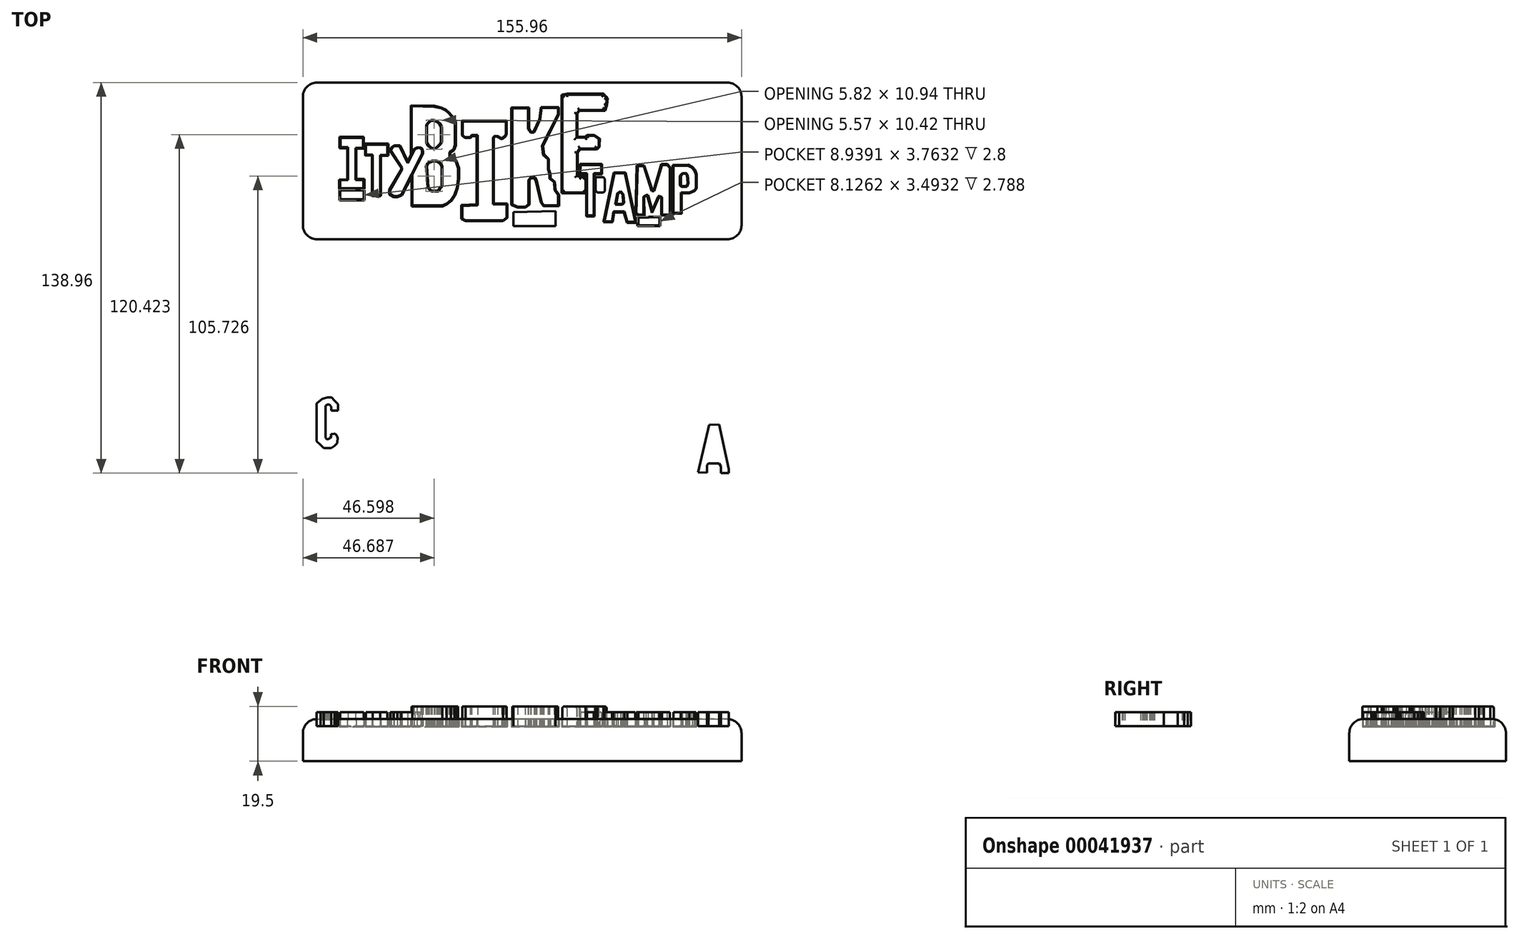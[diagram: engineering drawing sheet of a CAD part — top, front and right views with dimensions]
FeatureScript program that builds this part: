
annotation { "Feature Type Name" : "Feature", "Feature Type Description" : "" }
export const myFeature = defineFeature(function(context is Context, id is Id, definition is map)
    precondition{}
    {
        {
            var Q0;
            Q0=qCreatedBy(makeId("Top.planeOp"),FACE);
            var sketch = newSketch(context, id + "F0", { "sketchPlane" : qUnion([Q0])});
            skLineSegment(sketch, "E0", {"start": v(7.3, -128.71) * mm, "end": v(7.3, -128.71) * mm});
            skLineSegment(sketch, "E1", {"start": v(7.3, -128.71) * mm, "end": v(6.42, -129.66) * mm});
            skLineSegment(sketch, "E2", {"start": v(6.42, -129.66) * mm, "end": v(5.21, -130.33) * mm});
            skLineSegment(sketch, "E3", {"start": v(5.21, -130.33) * mm, "end": v(2.52, -130.33) * mm});
            skLineSegment(sketch, "E4", {"start": v(2.52, -130.33) * mm, "end": v(1.45, -129.25) * mm});
            skLineSegment(sketch, "E5", {"start": v(1.45, -129.25) * mm, "end": v(0, -127.97) * mm});
            skLineSegment(sketch, "E6", {"start": v(0, -127.97) * mm, "end": v(0, -127.17) * mm});
            skLineSegment(sketch, "E7", {"start": v(0, -127.17) * mm, "end": v(0, -114.52) * mm});
            skLineSegment(sketch, "E8", {"start": v(0, -114.52) * mm, "end": v(2.03, -112.78) * mm});
            skLineSegment(sketch, "E9", {"start": v(2.03, -112.78) * mm, "end": v(2.07, -112.78) * mm});
            skLineSegment(sketch, "E10", {"start": v(2.07, -112.78) * mm, "end": v(3.94, -112.3) * mm});
            skLineSegment(sketch, "E11", {"start": v(3.94, -112.3) * mm, "end": v(5.35, -112.3) * mm});
            skLineSegment(sketch, "E12", {"start": v(5.35, -112.3) * mm, "end": v(6.42, -113.45) * mm});
            skLineSegment(sketch, "E13", {"start": v(6.42, -113.45) * mm, "end": v(7.7, -114.73) * mm});
            skLineSegment(sketch, "E14", {"start": v(7.7, -114.73) * mm, "end": v(7.7, -116.34) * mm});
            skLineSegment(sketch, "E15", {"start": v(7.7, -116.34) * mm, "end": v(7.7, -117.01) * mm});
            skLineSegment(sketch, "E16", {"start": v(7.7, -117.01) * mm, "end": v(5.28, -117.01) * mm});
            skLineSegment(sketch, "E17", {"start": v(5.28, -117.01) * mm, "end": v(5.28, -115.6) * mm});
            skLineSegment(sketch, "E18", {"start": v(5.28, -115.6) * mm, "end": v(4.54, -114.9) * mm});
            skLineSegment(sketch, "E19", {"start": v(4.54, -114.9) * mm, "end": v(3.94, -114.9) * mm});
            skLineSegment(sketch, "E20", {"start": v(3.94, -114.9) * mm, "end": v(3.26, -115.27) * mm});
            skLineSegment(sketch, "E21", {"start": v(3.26, -115.27) * mm, "end": v(3.26, -115.7) * mm});
            skLineSegment(sketch, "E22", {"start": v(3.26, -115.7) * mm, "end": v(3.26, -126.66) * mm});
            skLineSegment(sketch, "E23", {"start": v(3.26, -126.66) * mm, "end": v(3.58, -127.14) * mm});
            skLineSegment(sketch, "E24", {"start": v(3.58, -127.14) * mm, "end": v(4.1, -127.14) * mm});
            skLineSegment(sketch, "E25", {"start": v(4.1, -127.14) * mm, "end": v(4.9, -126.82) * mm});
            skLineSegment(sketch, "E26", {"start": v(4.9, -126.82) * mm, "end": v(5.18, -126.18) * mm});
            skLineSegment(sketch, "E27", {"start": v(5.18, -126.18) * mm, "end": v(5.14, -125.38) * mm});
            skLineSegment(sketch, "E28", {"start": v(5.14, -125.38) * mm, "end": v(6.06, -125.34) * mm});
            skLineSegment(sketch, "E29", {"start": v(6.06, -125.34) * mm, "end": v(6.58, -125.34) * mm});
            skLineSegment(sketch, "E30", {"start": v(6.58, -125.34) * mm, "end": v(7.14, -125.82) * mm});
            skLineSegment(sketch, "E31", {"start": v(7.14, -125.82) * mm, "end": v(7.54, -126.82) * mm});
            skLineSegment(sketch, "E32", {"start": v(7.54, -126.82) * mm, "end": v(7.45, -128.26) * mm});
            skLineSegment(sketch, "E33", {"start": v(7.45, -128.26) * mm, "end": v(7.3, -128.71) * mm});
            skLineSegment(sketch, "E34", {"start": v(8.43, -38.73) * mm, "end": v(8.43, -41.9) * mm});
            skLineSegment(sketch, "E35", {"start": v(8.43, -41.9) * mm, "end": v(16.77, -41.9) * mm});
            skLineSegment(sketch, "E36", {"start": v(16.77, -41.9) * mm, "end": v(16.77, -38.8) * mm});
            skLineSegment(sketch, "E37", {"start": v(16.77, -38.8) * mm, "end": v(8.43, -38.73) * mm});
            skLineSegment(sketch, "E38", {"start": v(8.4, -35.1) * mm, "end": v(8.4, -37.86) * mm});
            skLineSegment(sketch, "E39", {"start": v(8.4, -37.86) * mm, "end": v(16.72, -37.86) * mm});
            skLineSegment(sketch, "E40", {"start": v(16.72, -37.86) * mm, "end": v(16.72, -34.97) * mm});
            skLineSegment(sketch, "E41", {"start": v(16.72, -34.97) * mm, "end": v(13.88, -34.97) * mm});
            skLineSegment(sketch, "E42", {"start": v(13.88, -34.97) * mm, "end": v(13.88, -23.55) * mm});
            skLineSegment(sketch, "E43", {"start": v(13.88, -23.55) * mm, "end": v(16.48, -23.55) * mm});
            skLineSegment(sketch, "E44", {"start": v(16.48, -23.55) * mm, "end": v(16.48, -19.95) * mm});
            skLineSegment(sketch, "E45", {"start": v(16.48, -19.95) * mm, "end": v(8.48, -19.95) * mm});
            skLineSegment(sketch, "E46", {"start": v(8.48, -19.95) * mm, "end": v(8.48, -23.35) * mm});
            skLineSegment(sketch, "E47", {"start": v(8.48, -23.35) * mm, "end": v(11.24, -23.35) * mm});
            skLineSegment(sketch, "E48", {"start": v(11.24, -23.35) * mm, "end": v(11.24, -34.99) * mm});
            skLineSegment(sketch, "E49", {"start": v(11.24, -34.99) * mm, "end": v(8.4, -35.1) * mm});
            skLineSegment(sketch, "E50", {"start": v(19.96, -25.92) * mm, "end": v(19.96, -40.42) * mm});
            skLineSegment(sketch, "E51", {"start": v(19.96, -40.42) * mm, "end": v(22.65, -40.42) * mm});
            skLineSegment(sketch, "E52", {"start": v(22.65, -40.42) * mm, "end": v(22.65, -26.04) * mm});
            skLineSegment(sketch, "E53", {"start": v(22.65, -26.04) * mm, "end": v(25.23, -26.04) * mm});
            skLineSegment(sketch, "E54", {"start": v(25.23, -26.04) * mm, "end": v(25.23, -22.39) * mm});
            skLineSegment(sketch, "E55", {"start": v(25.23, -22.39) * mm, "end": v(17.56, -22.39) * mm});
            skLineSegment(sketch, "E56", {"start": v(17.56, -22.39) * mm, "end": v(17.56, -25.98) * mm});
            skLineSegment(sketch, "E57", {"start": v(17.56, -25.98) * mm, "end": v(19.96, -25.92) * mm});
            skLineSegment(sketch, "E58", {"start": v(26.38, -24.56) * mm, "end": v(30.4, -30.61) * mm});
            skLineSegment(sketch, "E59", {"start": v(30.4, -30.61) * mm, "end": v(30.4, -31.35) * mm});
            skLineSegment(sketch, "E60", {"start": v(30.4, -31.35) * mm, "end": v(26.16, -38.64) * mm});
            skLineSegment(sketch, "E61", {"start": v(26.16, -38.64) * mm, "end": v(26.16, -39.89) * mm});
            skLineSegment(sketch, "E62", {"start": v(26.16, -39.89) * mm, "end": v(27.52, -40.73) * mm});
            skLineSegment(sketch, "E63", {"start": v(27.52, -40.73) * mm, "end": v(28.7, -40.73) * mm});
            skLineSegment(sketch, "E64", {"start": v(28.7, -40.73) * mm, "end": v(30.14, -40.16) * mm});
            skLineSegment(sketch, "E65", {"start": v(30.14, -40.16) * mm, "end": v(37.54, -25.76) * mm});
            skLineSegment(sketch, "E66", {"start": v(37.54, -25.76) * mm, "end": v(37.54, -24.3) * mm});
            skLineSegment(sketch, "E67", {"start": v(37.54, -24.3) * mm, "end": v(36.73, -23.6) * mm});
            skLineSegment(sketch, "E68", {"start": v(36.73, -23.6) * mm, "end": v(36.05, -23.6) * mm});
            skLineSegment(sketch, "E69", {"start": v(36.05, -23.6) * mm, "end": v(34.98, -24.05) * mm});
            skLineSegment(sketch, "E70", {"start": v(34.98, -24.05) * mm, "end": v(32.38, -28.97) * mm});
            skLineSegment(sketch, "E71", {"start": v(32.38, -28.97) * mm, "end": v(29.5, -22.92) * mm});
            skLineSegment(sketch, "E72", {"start": v(29.5, -22.92) * mm, "end": v(28.5, -22.92) * mm});
            skLineSegment(sketch, "E73", {"start": v(28.5, -22.92) * mm, "end": v(27.65, -22.92) * mm});
            skLineSegment(sketch, "E74", {"start": v(27.65, -22.92) * mm, "end": v(26.84, -23.64) * mm});
            skLineSegment(sketch, "E75", {"start": v(26.84, -23.64) * mm, "end": v(26.38, -24.56) * mm});
            skLineSegment(sketch, "E76", {"start": v(33.84, -8.7) * mm, "end": v(33.84, -25.36) * mm});
            skPoint(sketch, "E76.startSnap0", {"position": v(33.84, -32.96) * mm});
            skLineSegment(sketch, "E77", {"start": v(33.84, -25.36) * mm, "end": v(34.75, -23.9) * mm});
            skLineSegment(sketch, "E78", {"start": v(34.75, -23.9) * mm, "end": v(35.76, -23.4) * mm});
            skLineSegment(sketch, "E79", {"start": v(35.76, -23.4) * mm, "end": v(37.08, -23.4) * mm});
            skLineSegment(sketch, "E80", {"start": v(37.08, -23.4) * mm, "end": v(37.54, -23.71) * mm});
            skLineSegment(sketch, "E81", {"start": v(37.54, -23.71) * mm, "end": v(37.88, -24.87) * mm});
            skLineSegment(sketch, "E82", {"start": v(37.88, -24.87) * mm, "end": v(37.88, -25.61) * mm});
            skLineSegment(sketch, "E83", {"start": v(37.88, -25.61) * mm, "end": v(34.05, -32.96) * mm});
            skLineSegment(sketch, "E84", {"start": v(34.05, -32.96) * mm, "end": v(34.05, -44.03) * mm});
            skLineSegment(sketch, "E85", {"start": v(34.05, -44.03) * mm, "end": v(44.78, -44.03) * mm});
            skLineSegment(sketch, "E86", {"start": v(44.78, -44.03) * mm, "end": v(46.22, -43.31) * mm});
            skLineSegment(sketch, "E87", {"start": v(46.22, -43.31) * mm, "end": v(47.78, -42.11) * mm});
            skLineSegment(sketch, "E88", {"start": v(47.78, -42.11) * mm, "end": v(49.04, -40.26) * mm});
            skLineSegment(sketch, "E89", {"start": v(49.04, -40.26) * mm, "end": v(49.88, -37.68) * mm});
            skLineSegment(sketch, "E90", {"start": v(49.88, -37.68) * mm, "end": v(50.36, -34.5) * mm});
            skLineSegment(sketch, "E91", {"start": v(50.36, -34.5) * mm, "end": v(50.36, -30.8) * mm});
            skLineSegment(sketch, "E92", {"start": v(50.36, -30.8) * mm, "end": v(49.4, -28.15) * mm});
            skLineSegment(sketch, "E93", {"start": v(49.4, -28.15) * mm, "end": v(48.02, -26.78) * mm});
            skLineSegment(sketch, "E94", {"start": v(48.02, -26.78) * mm, "end": v(47.24, -26.78) * mm});
            skLineSegment(sketch, "E95", {"start": v(47.24, -26.78) * mm, "end": v(47.24, -25.04) * mm});
            skLineSegment(sketch, "E96", {"start": v(47.24, -25.04) * mm, "end": v(48.62, -24.14) * mm});
            skLineSegment(sketch, "E97", {"start": v(48.62, -24.14) * mm, "end": v(49.22, -22.58) * mm});
            skLineSegment(sketch, "E98", {"start": v(49.22, -22.58) * mm, "end": v(49.22, -14.31) * mm});
            skLineSegment(sketch, "E99", {"start": v(49.22, -14.31) * mm, "end": v(48.44, -12.88) * mm});
            skLineSegment(sketch, "E100", {"start": v(48.44, -12.88) * mm, "end": v(47, -11.2) * mm});
            skLineSegment(sketch, "E101", {"start": v(47, -11.2) * mm, "end": v(45.86, -10.24) * mm});
            skLineSegment(sketch, "E102", {"start": v(45.86, -10.24) * mm, "end": v(44.3, -9.46) * mm});
            skLineSegment(sketch, "E103", {"start": v(44.3, -9.46) * mm, "end": v(41.85, -8.92) * mm});
            skLineSegment(sketch, "E104", {"start": v(41.85, -8.92) * mm, "end": v(33.84, -8.7) * mm});
            skLineSegment(sketch, "E105", {"start": v(38.97, -15.33) * mm, "end": v(38.97, -21.8) * mm});
            skLineSegment(sketch, "E106", {"start": v(38.97, -21.8) * mm, "end": v(39.7, -22.88) * mm});
            skLineSegment(sketch, "E107", {"start": v(39.7, -22.88) * mm, "end": v(40.89, -23.78) * mm});
            skLineSegment(sketch, "E108", {"start": v(40.89, -23.78) * mm, "end": v(42.09, -24.08) * mm});
            skLineSegment(sketch, "E109", {"start": v(42.09, -24.08) * mm, "end": v(43.23, -23.18) * mm});
            skLineSegment(sketch, "E110", {"start": v(43.23, -23.18) * mm, "end": v(44.13, -22.28) * mm});
            skLineSegment(sketch, "E111", {"start": v(44.13, -22.28) * mm, "end": v(44.54, -21.44) * mm});
            skLineSegment(sketch, "E112", {"start": v(44.54, -21.44) * mm, "end": v(44.54, -16.11) * mm});
            skLineSegment(sketch, "E113", {"start": v(44.54, -16.11) * mm, "end": v(43.83, -14.8) * mm});
            skLineSegment(sketch, "E114", {"start": v(43.83, -14.8) * mm, "end": v(43.05, -14.2) * mm});
            skLineSegment(sketch, "E115", {"start": v(43.05, -14.2) * mm, "end": v(41.79, -13.65) * mm});
            skLineSegment(sketch, "E116", {"start": v(41.79, -13.65) * mm, "end": v(40.65, -13.65) * mm});
            skLineSegment(sketch, "E117", {"start": v(40.65, -13.65) * mm, "end": v(39.7, -14.5) * mm});
            skLineSegment(sketch, "E118", {"start": v(39.7, -14.5) * mm, "end": v(38.97, -15.33) * mm});
            skLineSegment(sketch, "E119", {"start": v(39.47, -37.6) * mm, "end": v(38.94, -30.01) * mm});
            skLineSegment(sketch, "E120", {"start": v(38.94, -30.01) * mm, "end": v(39.58, -28.84) * mm});
            skLineSegment(sketch, "E121", {"start": v(39.58, -28.84) * mm, "end": v(41.07, -28.1) * mm});
            skLineSegment(sketch, "E122", {"start": v(41.07, -28.1) * mm, "end": v(42.73, -28.1) * mm});
            skLineSegment(sketch, "E123", {"start": v(42.73, -28.1) * mm, "end": v(44.33, -29.16) * mm});
            skLineSegment(sketch, "E124", {"start": v(44.33, -29.16) * mm, "end": v(44.76, -30.17) * mm});
            skLineSegment(sketch, "E125", {"start": v(44.76, -30.17) * mm, "end": v(44.76, -37.33) * mm});
            skLineSegment(sketch, "E126", {"start": v(44.76, -37.33) * mm, "end": v(44.06, -37.91) * mm});
            skLineSegment(sketch, "E127", {"start": v(44.06, -37.91) * mm, "end": v(43.42, -39.04) * mm});
            skLineSegment(sketch, "E128", {"start": v(43.42, -39.04) * mm, "end": v(40.75, -39.04) * mm});
            skLineSegment(sketch, "E129", {"start": v(40.75, -39.04) * mm, "end": v(40.06, -38.34) * mm});
            skLineSegment(sketch, "E130", {"start": v(40.06, -38.34) * mm, "end": v(39.47, -37.6) * mm});
            skLineSegment(sketch, "E131", {"start": v(51.83, -44.2) * mm, "end": v(51.83, -48.63) * mm});
            skLineSegment(sketch, "E132", {"start": v(51.83, -48.63) * mm, "end": v(53.03, -49.35) * mm});
            skLineSegment(sketch, "E133", {"start": v(53.03, -49.35) * mm, "end": v(66.27, -49.35) * mm});
            skLineSegment(sketch, "E134", {"start": v(66.27, -49.35) * mm, "end": v(67.59, -48.33) * mm});
            skLineSegment(sketch, "E135", {"start": v(67.59, -48.33) * mm, "end": v(67.59, -43.66) * mm});
            skLineSegment(sketch, "E136", {"start": v(67.59, -43.66) * mm, "end": v(62.74, -43.66) * mm});
            skLineSegment(sketch, "E137", {"start": v(62.74, -43.66) * mm, "end": v(62.74, -19.81) * mm});
            skLineSegment(sketch, "E138", {"start": v(62.74, -19.81) * mm, "end": v(63.4, -19.21) * mm});
            skLineSegment(sketch, "E139", {"start": v(63.4, -19.21) * mm, "end": v(64.35, -19.33) * mm});
            skLineSegment(sketch, "E140", {"start": v(64.35, -19.33) * mm, "end": v(65.85, -20.17) * mm});
            skLineSegment(sketch, "E141", {"start": v(65.85, -20.17) * mm, "end": v(66.87, -19.4) * mm});
            skLineSegment(sketch, "E142", {"start": v(66.87, -19.4) * mm, "end": v(67.3, -18.73) * mm});
            skLineSegment(sketch, "E143", {"start": v(67.3, -18.73) * mm, "end": v(67.3, -14.18) * mm});
            skLineSegment(sketch, "E144", {"start": v(67.3, -14.18) * mm, "end": v(52.01, -14.18) * mm});
            skLineSegment(sketch, "E145", {"start": v(52.01, -14.18) * mm, "end": v(52.01, -19.03) * mm});
            skLineSegment(sketch, "E146", {"start": v(52.01, -19.03) * mm, "end": v(52.8, -19.7) * mm});
            skLineSegment(sketch, "E147", {"start": v(52.8, -19.7) * mm, "end": v(54.59, -19.7) * mm});
            skLineSegment(sketch, "E148", {"start": v(54.59, -19.7) * mm, "end": v(55.13, -19.03) * mm});
            skLineSegment(sketch, "E149", {"start": v(55.13, -19.03) * mm, "end": v(57.28, -19.03) * mm});
            skLineSegment(sketch, "E150", {"start": v(57.28, -19.03) * mm, "end": v(57.28, -43.24) * mm});
            skLineSegment(sketch, "E151", {"start": v(57.28, -43.24) * mm, "end": v(57.28, -43.96) * mm});
            skLineSegment(sketch, "E152", {"start": v(57.28, -43.96) * mm, "end": v(51.83, -44.2) * mm});
            skLineSegment(sketch, "E153", {"start": v(70, -46.39) * mm, "end": v(70, -51.38) * mm});
            skLineSegment(sketch, "E154", {"start": v(70, -51.38) * mm, "end": v(84.93, -51.38) * mm});
            skLineSegment(sketch, "E155", {"start": v(84.93, -51.38) * mm, "end": v(84.93, -46.06) * mm});
            skLineSegment(sketch, "E156", {"start": v(84.93, -46.06) * mm, "end": v(70, -46.39) * mm});
            skLineSegment(sketch, "E157", {"start": v(69.57, -43.68) * mm, "end": v(69.57, -9.49) * mm});
            skLineSegment(sketch, "E158", {"start": v(69.57, -9.49) * mm, "end": v(75.23, -9.49) * mm});
            skLineSegment(sketch, "E159", {"start": v(75.23, -9.49) * mm, "end": v(75.23, -15.86) * mm});
            skLineSegment(sketch, "E160", {"start": v(75.23, -15.86) * mm, "end": v(75.23, -16.76) * mm});
            skLineSegment(sketch, "E161", {"start": v(75.23, -16.76) * mm, "end": v(76.09, -18.1) * mm});
            skLineSegment(sketch, "E162", {"start": v(76.09, -18.1) * mm, "end": v(77.32, -18.1) * mm});
            skLineSegment(sketch, "E163", {"start": v(77.32, -18.1) * mm, "end": v(79.51, -13.34) * mm});
            skLineSegment(sketch, "E164", {"start": v(79.51, -13.34) * mm, "end": v(80.08, -9.4) * mm});
            skLineSegment(sketch, "E165", {"start": v(80.08, -9.4) * mm, "end": v(85.88, -9.4) * mm});
            skLineSegment(sketch, "E166", {"start": v(85.88, -9.4) * mm, "end": v(85.88, -11.63) * mm});
            skLineSegment(sketch, "E167", {"start": v(85.88, -11.63) * mm, "end": v(80.22, -22.76) * mm});
            skLineSegment(sketch, "E168", {"start": v(80.22, -22.76) * mm, "end": v(80.6, -26.04) * mm});
            skLineSegment(sketch, "E169", {"start": v(80.6, -26.04) * mm, "end": v(82.32, -27.6) * mm});
            skLineSegment(sketch, "E170", {"start": v(82.32, -27.6) * mm, "end": v(82.32, -31.22) * mm});
            skLineSegment(sketch, "E171", {"start": v(82.32, -31.22) * mm, "end": v(82.89, -32.84) * mm});
            skLineSegment(sketch, "E172", {"start": v(82.89, -32.84) * mm, "end": v(82.89, -34.45) * mm});
            skLineSegment(sketch, "E173", {"start": v(82.89, -34.45) * mm, "end": v(84.46, -35.74) * mm});
            skLineSegment(sketch, "E174", {"start": v(84.46, -35.74) * mm, "end": v(84.65, -38.6) * mm});
            skLineSegment(sketch, "E175", {"start": v(84.65, -38.6) * mm, "end": v(85.93, -40.3) * mm});
            skLineSegment(sketch, "E176", {"start": v(85.93, -40.3) * mm, "end": v(85.93, -43.96) * mm});
            skLineSegment(sketch, "E177", {"start": v(85.93, -43.96) * mm, "end": v(80.84, -43.96) * mm});
            skLineSegment(sketch, "E178", {"start": v(80.84, -43.96) * mm, "end": v(80.08, -42.87) * mm});
            skLineSegment(sketch, "E179", {"start": v(80.08, -42.87) * mm, "end": v(78.23, -34.93) * mm});
            skLineSegment(sketch, "E180", {"start": v(78.23, -34.93) * mm, "end": v(77.7, -34.03) * mm});
            skLineSegment(sketch, "E181", {"start": v(77.7, -34.03) * mm, "end": v(76.75, -34.03) * mm});
            skLineSegment(sketch, "E182", {"start": v(76.75, -34.03) * mm, "end": v(76.18, -34.03) * mm});
            skLineSegment(sketch, "E183", {"start": v(76.18, -34.03) * mm, "end": v(75.37, -34.93) * mm});
            skLineSegment(sketch, "E184", {"start": v(75.37, -34.93) * mm, "end": v(75.37, -43.63) * mm});
            skLineSegment(sketch, "E185", {"start": v(75.37, -43.63) * mm, "end": v(74.23, -44.49) * mm});
            skLineSegment(sketch, "E186", {"start": v(74.23, -44.49) * mm, "end": v(71.57, -44.49) * mm});
            skLineSegment(sketch, "E187", {"start": v(71.57, -44.49) * mm, "end": v(69.57, -43.68) * mm});
            skLineSegment(sketch, "E188", {"start": v(87.4, -4.91) * mm, "end": v(87.4, -39.4) * mm});
            skLineSegment(sketch, "E189", {"start": v(87.4, -39.4) * mm, "end": v(95.63, -39.4) * mm});
            skLineSegment(sketch, "E190", {"start": v(95.63, -39.4) * mm, "end": v(95.63, -33.97) * mm});
            skLineSegment(sketch, "E191", {"start": v(95.63, -33.97) * mm, "end": v(93.82, -33.97) * mm});
            skLineSegment(sketch, "E192", {"start": v(93.82, -33.97) * mm, "end": v(92.61, -33.52) * mm});
            skLineSegment(sketch, "E193", {"start": v(92.61, -33.52) * mm, "end": v(92.61, -25.3) * mm});
            skLineSegment(sketch, "E194", {"start": v(92.61, -25.3) * mm, "end": v(93.6, -23.7) * mm});
            skLineSegment(sketch, "E195", {"start": v(93.6, -23.7) * mm, "end": v(99.33, -23.78) * mm});
            skLineSegment(sketch, "E196", {"start": v(99.33, -23.78) * mm, "end": v(100.31, -23.25) * mm});
            skLineSegment(sketch, "E197", {"start": v(100.31, -23.25) * mm, "end": v(100.39, -20.39) * mm});
            skLineSegment(sketch, "E198", {"start": v(100.39, -20.39) * mm, "end": v(98.73, -19.25) * mm});
            skLineSegment(sketch, "E199", {"start": v(98.73, -19.25) * mm, "end": v(96.24, -19.25) * mm});
            skLineSegment(sketch, "E200", {"start": v(96.24, -19.25) * mm, "end": v(95.63, -19.86) * mm});
            skLineSegment(sketch, "E201", {"start": v(95.63, -19.86) * mm, "end": v(92.46, -19.86) * mm});
            skLineSegment(sketch, "E202", {"start": v(92.46, -19.86) * mm, "end": v(92.46, -11.33) * mm});
            skLineSegment(sketch, "E203", {"start": v(92.46, -11.33) * mm, "end": v(93.37, -10.04) * mm});
            skLineSegment(sketch, "E204", {"start": v(93.37, -10.04) * mm, "end": v(102.43, -10.04) * mm});
            skLineSegment(sketch, "E205", {"start": v(102.43, -10.04) * mm, "end": v(103.03, -8.23) * mm});
            skLineSegment(sketch, "E206", {"start": v(103.03, -8.23) * mm, "end": v(103.18, -5.97) * mm});
            skLineSegment(sketch, "E207", {"start": v(103.18, -5.97) * mm, "end": v(101.97, -4.6) * mm});
            skLineSegment(sketch, "E208", {"start": v(101.97, -4.6) * mm, "end": v(89.07, -4.6) * mm});
            skLineSegment(sketch, "E209", {"start": v(89.07, -4.6) * mm, "end": v(87.4, -4.91) * mm});
            skLineSegment(sketch, "E210", {"start": v(99.86, -39.47) * mm, "end": v(99.18, -38.64) * mm});
            skLineSegment(sketch, "E211", {"start": v(99.18, -38.64) * mm, "end": v(99.18, -34.03) * mm});
            skLineSegment(sketch, "E212", {"start": v(99.18, -34.03) * mm, "end": v(101.98, -34.03) * mm});
            skLineSegment(sketch, "E213", {"start": v(101.98, -34.03) * mm, "end": v(102.58, -34.6) * mm});
            skLineSegment(sketch, "E214", {"start": v(102.58, -34.6) * mm, "end": v(102.58, -38.94) * mm});
            skLineSegment(sketch, "E215", {"start": v(102.58, -38.94) * mm, "end": v(102.01, -39.43) * mm});
            skLineSegment(sketch, "E216", {"start": v(102.01, -39.43) * mm, "end": v(99.86, -39.47) * mm});
            skLineSegment(sketch, "E217", {"start": v(93.75, -32.52) * mm, "end": v(96.16, -32.52) * mm});
            skLineSegment(sketch, "E218", {"start": v(96.16, -32.52) * mm, "end": v(96.16, -47.58) * mm});
            skLineSegment(sketch, "E219", {"start": v(96.16, -47.58) * mm, "end": v(98.54, -47.58) * mm});
            skLineSegment(sketch, "E220", {"start": v(98.54, -47.58) * mm, "end": v(98.54, -32.63) * mm});
            skLineSegment(sketch, "E221", {"start": v(98.54, -32.63) * mm, "end": v(101.26, -32.63) * mm});
            skLineSegment(sketch, "E222", {"start": v(101.26, -32.63) * mm, "end": v(101.26, -29.61) * mm});
            skLineSegment(sketch, "E223", {"start": v(101.26, -29.61) * mm, "end": v(93.86, -29.61) * mm});
            skLineSegment(sketch, "E224", {"start": v(93.86, -29.61) * mm, "end": v(93.75, -32.52) * mm});
            skLineSegment(sketch, "E225", {"start": v(102.34, -49.66) * mm, "end": v(105.11, -49.66) * mm});
            skLineSegment(sketch, "E226", {"start": v(105.11, -49.66) * mm, "end": v(105.6, -46.2) * mm});
            skLineSegment(sketch, "E227", {"start": v(105.6, -46.2) * mm, "end": v(109.49, -46.2) * mm});
            skLineSegment(sketch, "E228", {"start": v(109.49, -46.2) * mm, "end": v(110.56, -49.88) * mm});
            skLineSegment(sketch, "E229", {"start": v(110.56, -49.88) * mm, "end": v(113.28, -49.88) * mm});
            skLineSegment(sketch, "E230", {"start": v(113.28, -49.88) * mm, "end": v(109.6, -32.58) * mm});
            skLineSegment(sketch, "E231", {"start": v(109.6, -32.58) * mm, "end": v(105.96, -32.58) * mm});
            skLineSegment(sketch, "E232", {"start": v(105.96, -32.58) * mm, "end": v(102.34, -49.66) * mm});
            skLineSegment(sketch, "E233", {"start": v(106.18, -43.74) * mm, "end": v(108.8, -43.74) * mm});
            skLineSegment(sketch, "E234", {"start": v(108.8, -43.74) * mm, "end": v(109.33, -43.15) * mm});
            skLineSegment(sketch, "E235", {"start": v(109.33, -43.15) * mm, "end": v(109.17, -40.05) * mm});
            skLineSegment(sketch, "E236", {"start": v(109.17, -40.05) * mm, "end": v(108.1, -38.88) * mm});
            skLineSegment(sketch, "E237", {"start": v(108.1, -38.88) * mm, "end": v(106.93, -39.68) * mm});
            skLineSegment(sketch, "E238", {"start": v(106.93, -39.68) * mm, "end": v(106.18, -43.74) * mm});
            skLineSegment(sketch, "E239", {"start": v(114.4, -48.49) * mm, "end": v(114.4, -51.1) * mm});
            skLineSegment(sketch, "E240", {"start": v(114.4, -51.1) * mm, "end": v(121.92, -51.1) * mm});
            skLineSegment(sketch, "E241", {"start": v(121.92, -51.1) * mm, "end": v(121.92, -48.22) * mm});
            skLineSegment(sketch, "E242", {"start": v(121.92, -48.22) * mm, "end": v(114.4, -48.49) * mm});
            skLineSegment(sketch, "E243", {"start": v(113.7, -46.67) * mm, "end": v(114.4, -47.37) * mm});
            skLineSegment(sketch, "E244", {"start": v(114.4, -47.37) * mm, "end": v(116.27, -47.37) * mm});
            skLineSegment(sketch, "E245", {"start": v(116.27, -47.37) * mm, "end": v(116.21, -41.02) * mm});
            skLineSegment(sketch, "E246", {"start": v(116.21, -41.02) * mm, "end": v(117.07, -40.37) * mm});
            skLineSegment(sketch, "E247", {"start": v(117.07, -40.37) * mm, "end": v(117.87, -40.37) * mm});
            skLineSegment(sketch, "E248", {"start": v(117.87, -40.37) * mm, "end": v(119.36, -45.77) * mm});
            skLineSegment(sketch, "E249", {"start": v(119.36, -45.77) * mm, "end": v(121.44, -41.02) * mm});
            skLineSegment(sketch, "E250", {"start": v(121.44, -41.02) * mm, "end": v(122.14, -40.54) * mm});
            skLineSegment(sketch, "E251", {"start": v(122.14, -40.54) * mm, "end": v(122.83, -41.12) * mm});
            skLineSegment(sketch, "E252", {"start": v(122.83, -41.12) * mm, "end": v(122.83, -47.31) * mm});
            skLineSegment(sketch, "E253", {"start": v(122.83, -47.31) * mm, "end": v(125.6, -47.31) * mm});
            skLineSegment(sketch, "E254", {"start": v(125.6, -47.31) * mm, "end": v(125.6, -30.66) * mm});
            skLineSegment(sketch, "E255", {"start": v(125.6, -30.66) * mm, "end": v(124.6, -29.6) * mm});
            skLineSegment(sketch, "E256", {"start": v(124.6, -29.6) * mm, "end": v(122.78, -29.6) * mm});
            skLineSegment(sketch, "E257", {"start": v(122.78, -29.6) * mm, "end": v(120.1, -38.88) * mm});
            skLineSegment(sketch, "E258", {"start": v(120.1, -38.88) * mm, "end": v(119.16, -38.88) * mm});
            skLineSegment(sketch, "E259", {"start": v(119.16, -38.88) * mm, "end": v(116.32, -30.08) * mm});
            skLineSegment(sketch, "E260", {"start": v(116.32, -30.08) * mm, "end": v(114.16, -30.08) * mm});
            skLineSegment(sketch, "E261", {"start": v(114.16, -30.08) * mm, "end": v(113.7, -46.67) * mm});
            skLineSegment(sketch, "E262", {"start": v(126.94, -46.62) * mm, "end": v(126.94, -29.9) * mm});
            skLineSegment(sketch, "E263", {"start": v(126.94, -29.9) * mm, "end": v(132.15, -29.85) * mm});
            skLineSegment(sketch, "E264", {"start": v(132.15, -29.85) * mm, "end": v(133.4, -30.57) * mm});
            skLineSegment(sketch, "E265", {"start": v(133.4, -30.57) * mm, "end": v(134.43, -31.65) * mm});
            skLineSegment(sketch, "E266", {"start": v(134.43, -31.65) * mm, "end": v(134.9, -33.02) * mm});
            skLineSegment(sketch, "E267", {"start": v(134.9, -33.02) * mm, "end": v(134.9, -37.88) * mm});
            skLineSegment(sketch, "E268", {"start": v(134.9, -37.88) * mm, "end": v(134.25, -38.72) * mm});
            skLineSegment(sketch, "E269", {"start": v(134.25, -38.72) * mm, "end": v(132.57, -39.38) * mm});
            skLineSegment(sketch, "E270", {"start": v(132.57, -39.38) * mm, "end": v(129.51, -39.38) * mm});
            skLineSegment(sketch, "E271", {"start": v(129.51, -39.38) * mm, "end": v(129.51, -46.68) * mm});
            skLineSegment(sketch, "E272", {"start": v(129.51, -46.68) * mm, "end": v(126.94, -46.62) * mm});
            skLineSegment(sketch, "E273", {"start": v(135.68, -139) * mm, "end": v(139.58, -122.16) * mm});
            skLineSegment(sketch, "E274", {"start": v(139.58, -122.16) * mm, "end": v(143.11, -122.04) * mm});
            skLineSegment(sketch, "E275", {"start": v(143.11, -122.04) * mm, "end": v(146.6, -137.86) * mm});
            skLineSegment(sketch, "E276", {"start": v(146.6, -137.86) * mm, "end": v(146.59, -139.3) * mm});
            skLineSegment(sketch, "E277", {"start": v(146.59, -139.3) * mm, "end": v(143.77, -139.26) * mm});
            skLineSegment(sketch, "E278", {"start": v(143.77, -139.26) * mm, "end": v(143.77, -136.9) * mm});
            skLineSegment(sketch, "E279", {"start": v(143.77, -136.9) * mm, "end": v(143.17, -135.88) * mm});
            skLineSegment(sketch, "E280", {"start": v(143.17, -135.88) * mm, "end": v(139.34, -135.88) * mm});
            skLineSegment(sketch, "E281", {"start": v(139.34, -135.88) * mm, "end": v(138.8, -136.48) * mm});
            skLineSegment(sketch, "E282", {"start": v(138.8, -136.48) * mm, "end": v(138.8, -139.11) * mm});
            skLineSegment(sketch, "E283", {"start": v(138.8, -139.11) * mm, "end": v(135.68, -139) * mm});
            skLineSegment(sketch, "E284", {"start": v(139.88, -43.57) * mm, "end": v(139.88, -40.57) * mm});
            skLineSegment(sketch, "E285", {"start": v(139.88, -40.57) * mm, "end": v(140.84, -39.2) * mm});
            skLineSegment(sketch, "E286", {"start": v(140.84, -39.2) * mm, "end": v(142.28, -39.08) * mm});
            skLineSegment(sketch, "E287", {"start": v(142.28, -39.08) * mm, "end": v(143, -41.71) * mm});
            skLineSegment(sketch, "E288", {"start": v(143, -41.71) * mm, "end": v(142.4, -43.8) * mm});
            skLineSegment(sketch, "E289", {"start": v(142.4, -43.8) * mm, "end": v(139.88, -43.8) * mm});
            skLineSegment(sketch, "E290", {"start": v(139.88, -43.8) * mm, "end": v(139.88, -43.57) * mm});
            skLineSegment(sketch, "E291", {"start": v(129.2, -36.91) * mm, "end": v(129.2, -33.5) * mm});
            skLineSegment(sketch, "E292", {"start": v(129.2, -33.5) * mm, "end": v(130.05, -32.55) * mm});
            skLineSegment(sketch, "E293", {"start": v(130.05, -32.55) * mm, "end": v(131.39, -32.4) * mm});
            skLineSegment(sketch, "E294", {"start": v(131.39, -32.4) * mm, "end": v(132.04, -33.18) * mm});
            skLineSegment(sketch, "E295", {"start": v(132.04, -33.18) * mm, "end": v(132.3, -36.19) * mm});
            skLineSegment(sketch, "E296", {"start": v(132.3, -36.19) * mm, "end": v(131.76, -37.42) * mm});
            skLineSegment(sketch, "E297", {"start": v(131.76, -37.42) * mm, "end": v(129.95, -37.5) * mm});
            skLineSegment(sketch, "E298", {"start": v(129.95, -37.5) * mm, "end": v(129.2, -36.91) * mm});
            skSolve(sketch);
        }
        {
            var Q0;
            Q0=makeQuery(id+"F0.imprint","IMPRINT",FACE,{"disambiguationData":[TD([[makeQuery(id+"F0.imprint","IMPRINT",EDGE,{"derivedFrom":sQuery(id+"F0.wireOp",EDGE,"E1")}),-1.0]])]});
            var Q1;
            Q1=makeQuery(id+"F0.imprint","IMPRINT",FACE,{"disambiguationData":[TD([[makeQuery(id+"F0.imprint","IMPRINT",EDGE,{"derivedFrom":sQuery(id+"F0.wireOp",EDGE,"E38")}),1.0]])]});
            var Q2;
            Q2=makeQuery(id+"F0.imprint","IMPRINT",FACE,{"disambiguationData":[TD([[makeQuery(id+"F0.imprint","IMPRINT",EDGE,{"derivedFrom":sQuery(id+"F0.wireOp",EDGE,"E34")}),1.0]])]});
            var Q3;
            Q3=makeQuery(id+"F0.imprint","IMPRINT",FACE,{"disambiguationData":[TD([[makeQuery(id+"F0.imprint","IMPRINT",EDGE,{"derivedFrom":sQuery(id+"F0.wireOp",EDGE,"E50")}),1.0]])]});
            var Q4;
            Q4=makeQuery(id+"F0.imprint","IMPRINT",FACE,{"disambiguationData":[TD([[makeQuery(id+"F0.imprint","IMPRINT",EDGE,{"derivedFrom":sQuery(id+"F0.wireOp",EDGE,"E58")}),1.0]])]});
            var Q5;
            Q5=makeQuery(id+"F0.imprint","IMPRINT",FACE,{"disambiguationData":[TD([[makeQuery(id+"F0.imprint","IMPRINT",EDGE,{"derivedFrom":sQuery(id+"F0.wireOp",EDGE,"E217")}),1.0]])]});
            var Q6;
            Q6=makeQuery(id+"F0.imprint","IMPRINT",FACE,{"disambiguationData":[TD([[makeQuery(id+"F0.imprint","IMPRINT",EDGE,{"derivedFrom":sQuery(id+"F0.wireOp",EDGE,"E225")}),1.0]])]});
            var Q7;
            Q7=makeQuery(id+"F0.imprint","IMPRINT",FACE,{"disambiguationData":[TD([[makeQuery(id+"F0.imprint","IMPRINT",EDGE,{"derivedFrom":sQuery(id+"F0.wireOp",EDGE,"E243")}),1.0]])]});
            var Q8;
            Q8=makeQuery(id+"F0.imprint","IMPRINT",FACE,{"disambiguationData":[TD([[makeQuery(id+"F0.imprint","IMPRINT",EDGE,{"derivedFrom":sQuery(id+"F0.wireOp",EDGE,"E239")}),1.0]])]});
            var Q9;
            Q9=makeQuery(id+"F0.imprint","IMPRINT",FACE,{"disambiguationData":[TD([[makeQuery(id+"F0.imprint","IMPRINT",EDGE,{"derivedFrom":sQuery(id+"F0.wireOp",EDGE,"E262")}),-1.0]])]});
            var Q10;
            Q10=makeQuery(id+"F0.imprint","IMPRINT",FACE,{"disambiguationData":[TD([[makeQuery(id+"F0.imprint","IMPRINT",EDGE,{"derivedFrom":sQuery(id+"F0.wireOp",EDGE,"E273")}),-1.0]])]});
            extrude(context, id + "F1", {"entities" : qUnion([Q0, Q1, Q2, Q3, Q4, Q5, Q6, Q7, Q8, Q9, Q10]), "depth" : 5 * mm});
        }
        {
            var Q0;
            Q0=makeQuery(id+"F0.imprint","IMPRINT",FACE,{"disambiguationData":[TD([[makeQuery(id+"F0.imprint","IMPRINT",EDGE,{"derivedFrom":sQuery(id+"F0.wireOp",EDGE,"E76")}),1.0]])]});
            var Q1;
            Q1=makeQuery(id+"F0.imprint","IMPRINT",FACE,{"disambiguationData":[TD([[makeQuery(id+"F0.imprint","IMPRINT",EDGE,{"derivedFrom":sQuery(id+"F0.wireOp",EDGE,"E131")}),1.0]])]});
            var Q2;
            Q2=makeQuery(id+"F0.imprint","IMPRINT",FACE,{"disambiguationData":[TD([[makeQuery(id+"F0.imprint","IMPRINT",EDGE,{"derivedFrom":sQuery(id+"F0.wireOp",EDGE,"E157")}),-1.0]])]});
            var Q3;
            Q3=makeQuery(id+"F0.imprint","IMPRINT",FACE,{"disambiguationData":[TD([[makeQuery(id+"F0.imprint","IMPRINT",EDGE,{"derivedFrom":sQuery(id+"F0.wireOp",EDGE,"E153")}),1.0]])]});
            var Q4;
            Q4=makeQuery(id+"F0.imprint","IMPRINT",FACE,{"disambiguationData":[TD([[makeQuery(id+"F0.imprint","IMPRINT",EDGE,{"derivedFrom":sQuery(id+"F0.wireOp",EDGE,"E188")}),1.0]])]});
            var Q5;
            Q5=makeQuery(id+"F0.imprint","IMPRINT",FACE,{"disambiguationData":[TD([[makeQuery(id+"F0.imprint","IMPRINT",EDGE,{"derivedFrom":sQuery(id+"F0.wireOp",EDGE,"E210")}),-1.0]])]});
            extrude(context, id + "F2", {"entities" : qUnion([Q0, Q1, Q2, Q3, Q4, Q5]), "depth" : 7 * mm});
        }
        {
            var Q0;
            Q0=makeQuery(id+"F2.opExtrude","CAP_EDGE",EDGE,{"disambiguationData":[OSD([sQuery(id+"F0.wireOp",EDGE,"E204")])],"isStart":false});
            var Q1;
            Q1=makeQuery(id+"F2.opExtrude","CAP_EDGE",EDGE,{"disambiguationData":[OSD([sQuery(id+"F0.wireOp",EDGE,"E205")])],"isStart":false});
            var Q2;
            Q2=makeQuery(id+"F2.opExtrude","CAP_EDGE",EDGE,{"disambiguationData":[OSD([sQuery(id+"F0.wireOp",EDGE,"E206")])],"isStart":false});
            var Q3;
            Q3=makeQuery(id+"F2.opExtrude","CAP_EDGE",EDGE,{"disambiguationData":[OSD([sQuery(id+"F0.wireOp",EDGE,"E207")])],"isStart":false});
            var Q4;
            Q4=makeQuery(id+"F2.opExtrude","CAP_EDGE",EDGE,{"disambiguationData":[OSD([sQuery(id+"F0.wireOp",EDGE,"E208")])],"isStart":false});
            var Q5;
            Q5=makeQuery(id+"F2.opExtrude","CAP_EDGE",EDGE,{"disambiguationData":[OSD([sQuery(id+"F0.wireOp",EDGE,"E209")])],"isStart":false});
            var Q6;
            Q6=makeQuery(id+"F2.opExtrude","CAP_EDGE",EDGE,{"disambiguationData":[OSD([sQuery(id+"F0.wireOp",EDGE,"E188")])],"isStart":false});
            var Q7;
            Q7=makeQuery(id+"F2.opExtrude","CAP_EDGE",EDGE,{"disambiguationData":[OSD([sQuery(id+"F0.wireOp",EDGE,"E189")])],"isStart":false});
            var Q8;
            Q8=makeQuery(id+"F2.opExtrude","CAP_EDGE",EDGE,{"disambiguationData":[OSD([sQuery(id+"F0.wireOp",EDGE,"E190")])],"isStart":false});
            var Q9;
            Q9=makeQuery(id+"F2.opExtrude","CAP_EDGE",EDGE,{"disambiguationData":[OSD([sQuery(id+"F0.wireOp",EDGE,"E191")])],"isStart":false});
            var Q10;
            Q10=makeQuery(id+"F2.opExtrude","CAP_EDGE",EDGE,{"disambiguationData":[OSD([sQuery(id+"F0.wireOp",EDGE,"E192")])],"isStart":false});
            var Q11;
            Q11=makeQuery(id+"F2.opExtrude","CAP_EDGE",EDGE,{"disambiguationData":[OSD([sQuery(id+"F0.wireOp",EDGE,"E193")])],"isStart":false});
            var Q12;
            Q12=makeQuery(id+"F2.opExtrude","CAP_EDGE",EDGE,{"disambiguationData":[OSD([sQuery(id+"F0.wireOp",EDGE,"E194")])],"isStart":false});
            var Q13;
            Q13=makeQuery(id+"F2.opExtrude","CAP_EDGE",EDGE,{"disambiguationData":[OSD([sQuery(id+"F0.wireOp",EDGE,"E195")])],"isStart":false});
            var Q14;
            Q14=makeQuery(id+"F2.opExtrude","SWEPT_EDGE",EDGE,{"disambiguationData":[OSD([sQuery(id+"F0.wireOp",EDGE,"E196"),sQuery(id+"F0.wireOp",EDGE,"E197")])]});
            var Q15;
            Q15=makeQuery(id+"F2.opExtrude","CAP_EDGE",EDGE,{"disambiguationData":[OSD([sQuery(id+"F0.wireOp",EDGE,"E197")])],"isStart":false});
            var Q16;
            Q16=makeQuery(id+"F2.opExtrude","CAP_EDGE",EDGE,{"disambiguationData":[OSD([sQuery(id+"F0.wireOp",EDGE,"E199")])],"isStart":false});
            var Q17;
            Q17=makeQuery(id+"F2.opExtrude","CAP_EDGE",EDGE,{"disambiguationData":[OSD([sQuery(id+"F0.wireOp",EDGE,"E196")])],"isStart":false});
            var Q18;
            Q18=makeQuery(id+"F2.opExtrude","CAP_EDGE",EDGE,{"disambiguationData":[OSD([sQuery(id+"F0.wireOp",EDGE,"E200")])],"isStart":false});
            var Q19;
            Q19=makeQuery(id+"F2.opExtrude","CAP_EDGE",EDGE,{"disambiguationData":[OSD([sQuery(id+"F0.wireOp",EDGE,"E201")])],"isStart":false});
            var Q20;
            Q20=makeQuery(id+"F2.opExtrude","CAP_EDGE",EDGE,{"disambiguationData":[OSD([sQuery(id+"F0.wireOp",EDGE,"E202")])],"isStart":false});
            var Q21;
            Q21=makeQuery(id+"F2.opExtrude","CAP_EDGE",EDGE,{"disambiguationData":[OSD([sQuery(id+"F0.wireOp",EDGE,"E203")])],"isStart":false});
            fillet(context, id + "F3", {"entities" : qUnion([Q0, Q1, Q2, Q3, Q4, Q5, Q6, Q7, Q8, Q9, Q10, Q11, Q12, Q13, Q14, Q15, Q16, Q17, Q18, Q19, Q20, Q21]), "radius" : .75 * mm, "tangentPropagation" : true, "allowEdgeOverflow" : false});
        }
        {
            var Q0;
            Q0=qCreatedBy(makeId("Top.planeOp"),FACE);
            var sketch = newSketch(context, id + "F4", { "sketchPlane" : qUnion([Q0])});
            skLineSegment(sketch, "E299.rect.top", {"start": v(146.12, -0.33) * mm, "end": v(0.16, -0.33) * mm});
            skLineSegment(sketch, "E299.rect.left", {"start": v(151.12, -51.06) * mm, "end": v(151.12, -5.33) * mm});
            skLineSegment(sketch, "E299.rect.right", {"start": v(-4.84, -51.06) * mm, "end": v(-4.84, -5.33) * mm});
            skPoint(sketch, "E299.rect.middle", {"position": v(73.14, -37.12) * mm});
            skLineSegment(sketch, "E300", {"start": v(0.16, -56.06) * mm, "end": v(146.12, -56.06) * mm});
            skPoint(sketch, "E301.orphan", {"position": v(151.12, -73.9) * mm});
            skPoint(sketch, "E302.orphan", {"position": v(-4.84, -73.9) * mm});
            skPoint(sketch, "E303.visualSharp", {"position": v(-4.84, -0.33) * mm});
            skArc(sketch, "E303.filletArc", {"start": v(0.16, -0.33) * mm, "mid": v(-3.37, -1.8) * mm, "end": v(-4.84, -5.33) * mm});
            skPoint(sketch, "E304.visualSharp", {"position": v(-4.84, -56.06) * mm});
            skArc(sketch, "E304.filletArc", {"start": v(-4.84, -51.06) * mm, "mid": v(-3.37, -54.6) * mm, "end": v(0.16, -56.06) * mm});
            skPoint(sketch, "E305.visualSharp", {"position": v(151.12, -56.06) * mm});
            skArc(sketch, "E305.filletArc", {"start": v(146.12, -56.06) * mm, "mid": v(149.66, -54.6) * mm, "end": v(151.12, -51.06) * mm});
            skPoint(sketch, "E306.visualSharp", {"position": v(151.12, -0.33) * mm});
            skArc(sketch, "E306.filletArc", {"start": v(151.12, -5.33) * mm, "mid": v(149.66, -1.8) * mm, "end": v(146.12, -0.33) * mm});
            skSolve(sketch);
        }
        {
            var Q0;
            Q0 = qSketchRegion(id + "F4", true);
            extrude(context, id + "F5", {"entities" : qUnion([Q0]), "endBound" : BoundingType.SYMMETRIC, "oppositeDirection" : true, "depth" : 5 * mm});
        }
        {
            var Q0;
            Q0=makeQuery(id+"F5.opExtrude","CAP_FACE",FACE,{"disambiguationData":[OSD([sQuery(id+"F4.wireOp",EDGE,"E299.rect.top"),sQuery(id+"F4.wireOp",EDGE,"E299.rect.left"),sQuery(id+"F4.wireOp",EDGE,"E299.rect.right"),sQuery(id+"F4.wireOp",EDGE,"E300"),sQuery(id+"F4.wireOp",EDGE,"E303.filletArc"),sQuery(id+"F4.wireOp",EDGE,"E304.filletArc"),sQuery(id+"F4.wireOp",EDGE,"E305.filletArc"),sQuery(id+"F4.wireOp",EDGE,"E306.filletArc")])],"isStart":false});
            extrude(context, id + "F6", {"entities" : qUnion([Q0]), "operationType" : NewBodyOperationType.ADD, "depth" : 10 * mm});
        }
        {
            var Q0;
            Q0=makeQuery(id+"F1.opExtrude","SWEPT_BODY",BODY,{"disambiguationData":[OSD([sQuery(id+"F0.wireOp",EDGE,"E1"),sQuery(id+"F0.wireOp",EDGE,"E2"),sQuery(id+"F0.wireOp",EDGE,"E3"),sQuery(id+"F0.wireOp",EDGE,"E4"),sQuery(id+"F0.wireOp",EDGE,"E5"),sQuery(id+"F0.wireOp",EDGE,"E6"),sQuery(id+"F0.wireOp",EDGE,"E7"),sQuery(id+"F0.wireOp",EDGE,"E8"),sQuery(id+"F0.wireOp",EDGE,"E9"),sQuery(id+"F0.wireOp",EDGE,"E10"),sQuery(id+"F0.wireOp",EDGE,"E11"),sQuery(id+"F0.wireOp",EDGE,"E12"),sQuery(id+"F0.wireOp",EDGE,"E13"),sQuery(id+"F0.wireOp",EDGE,"E14"),sQuery(id+"F0.wireOp",EDGE,"E15"),sQuery(id+"F0.wireOp",EDGE,"E16"),sQuery(id+"F0.wireOp",EDGE,"E17"),sQuery(id+"F0.wireOp",EDGE,"E18"),sQuery(id+"F0.wireOp",EDGE,"E19"),sQuery(id+"F0.wireOp",EDGE,"E20"),sQuery(id+"F0.wireOp",EDGE,"E21"),sQuery(id+"F0.wireOp",EDGE,"E22"),sQuery(id+"F0.wireOp",EDGE,"E23"),sQuery(id+"F0.wireOp",EDGE,"E24"),sQuery(id+"F0.wireOp",EDGE,"E25"),sQuery(id+"F0.wireOp",EDGE,"E26"),sQuery(id+"F0.wireOp",EDGE,"E27"),sQuery(id+"F0.wireOp",EDGE,"E28"),sQuery(id+"F0.wireOp",EDGE,"E29"),sQuery(id+"F0.wireOp",EDGE,"E30"),sQuery(id+"F0.wireOp",EDGE,"E31"),sQuery(id+"F0.wireOp",EDGE,"E32"),sQuery(id+"F0.wireOp",EDGE,"E33")])]});
            var Q1;
            Q1=makeQuery(id+"F1.opExtrude","SWEPT_BODY",BODY,{"disambiguationData":[OSD([sQuery(id+"F0.wireOp",EDGE,"E38"),sQuery(id+"F0.wireOp",EDGE,"E39"),sQuery(id+"F0.wireOp",EDGE,"E40"),sQuery(id+"F0.wireOp",EDGE,"E41"),sQuery(id+"F0.wireOp",EDGE,"E42"),sQuery(id+"F0.wireOp",EDGE,"E43"),sQuery(id+"F0.wireOp",EDGE,"E44"),sQuery(id+"F0.wireOp",EDGE,"E45"),sQuery(id+"F0.wireOp",EDGE,"E46"),sQuery(id+"F0.wireOp",EDGE,"E47"),sQuery(id+"F0.wireOp",EDGE,"E48"),sQuery(id+"F0.wireOp",EDGE,"E49")])]});
            var Q2;
            Q2=makeQuery(id+"F1.opExtrude","SWEPT_BODY",BODY,{"disambiguationData":[OSD([sQuery(id+"F0.wireOp",EDGE,"E34"),sQuery(id+"F0.wireOp",EDGE,"E35"),sQuery(id+"F0.wireOp",EDGE,"E36"),sQuery(id+"F0.wireOp",EDGE,"E37")])]});
            var Q3;
            Q3=makeQuery(id+"F1.opExtrude","SWEPT_BODY",BODY,{"disambiguationData":[OSD([sQuery(id+"F0.wireOp",EDGE,"E50"),sQuery(id+"F0.wireOp",EDGE,"E51"),sQuery(id+"F0.wireOp",EDGE,"E52"),sQuery(id+"F0.wireOp",EDGE,"E53"),sQuery(id+"F0.wireOp",EDGE,"E54"),sQuery(id+"F0.wireOp",EDGE,"E55"),sQuery(id+"F0.wireOp",EDGE,"E56"),sQuery(id+"F0.wireOp",EDGE,"E57")])]});
            var Q4;
            Q4=makeQuery(id+"F1.opExtrude","SWEPT_BODY",BODY,{"disambiguationData":[OSD([sQuery(id+"F0.wireOp",EDGE,"E58"),sQuery(id+"F0.wireOp",EDGE,"E59"),sQuery(id+"F0.wireOp",EDGE,"E60"),sQuery(id+"F0.wireOp",EDGE,"E61"),sQuery(id+"F0.wireOp",EDGE,"E62"),sQuery(id+"F0.wireOp",EDGE,"E63"),sQuery(id+"F0.wireOp",EDGE,"E64"),sQuery(id+"F0.wireOp",EDGE,"E65"),sQuery(id+"F0.wireOp",EDGE,"E66"),sQuery(id+"F0.wireOp",EDGE,"E67"),sQuery(id+"F0.wireOp",EDGE,"E68"),sQuery(id+"F0.wireOp",EDGE,"E69"),sQuery(id+"F0.wireOp",EDGE,"E70"),sQuery(id+"F0.wireOp",EDGE,"E71"),sQuery(id+"F0.wireOp",EDGE,"E72"),sQuery(id+"F0.wireOp",EDGE,"E73"),sQuery(id+"F0.wireOp",EDGE,"E74"),sQuery(id+"F0.wireOp",EDGE,"E75")])]});
            var Q5;
            Q5=makeQuery(id+"F2.opExtrude","SWEPT_BODY",BODY,{"disambiguationData":[OSD([sQuery(id+"F0.wireOp",EDGE,"E76"),sQuery(id+"F0.wireOp",EDGE,"E77"),sQuery(id+"F0.wireOp",EDGE,"E78"),sQuery(id+"F0.wireOp",EDGE,"E79"),sQuery(id+"F0.wireOp",EDGE,"E80"),sQuery(id+"F0.wireOp",EDGE,"E81"),sQuery(id+"F0.wireOp",EDGE,"E82"),sQuery(id+"F0.wireOp",EDGE,"E83"),sQuery(id+"F0.wireOp",EDGE,"E84"),sQuery(id+"F0.wireOp",EDGE,"E85"),sQuery(id+"F0.wireOp",EDGE,"E86"),sQuery(id+"F0.wireOp",EDGE,"E87"),sQuery(id+"F0.wireOp",EDGE,"E88"),sQuery(id+"F0.wireOp",EDGE,"E89"),sQuery(id+"F0.wireOp",EDGE,"E90"),sQuery(id+"F0.wireOp",EDGE,"E91"),sQuery(id+"F0.wireOp",EDGE,"E92"),sQuery(id+"F0.wireOp",EDGE,"E93"),sQuery(id+"F0.wireOp",EDGE,"E94"),sQuery(id+"F0.wireOp",EDGE,"E95"),sQuery(id+"F0.wireOp",EDGE,"E96"),sQuery(id+"F0.wireOp",EDGE,"E97"),sQuery(id+"F0.wireOp",EDGE,"E98"),sQuery(id+"F0.wireOp",EDGE,"E99"),sQuery(id+"F0.wireOp",EDGE,"E100"),sQuery(id+"F0.wireOp",EDGE,"E101"),sQuery(id+"F0.wireOp",EDGE,"E102"),sQuery(id+"F0.wireOp",EDGE,"E103"),sQuery(id+"F0.wireOp",EDGE,"E104"),sQuery(id+"F0.wireOp",EDGE,"E105"),sQuery(id+"F0.wireOp",EDGE,"E106"),sQuery(id+"F0.wireOp",EDGE,"E107"),sQuery(id+"F0.wireOp",EDGE,"E108"),sQuery(id+"F0.wireOp",EDGE,"E109"),sQuery(id+"F0.wireOp",EDGE,"E110"),sQuery(id+"F0.wireOp",EDGE,"E111"),sQuery(id+"F0.wireOp",EDGE,"E112"),sQuery(id+"F0.wireOp",EDGE,"E113"),sQuery(id+"F0.wireOp",EDGE,"E114"),sQuery(id+"F0.wireOp",EDGE,"E115"),sQuery(id+"F0.wireOp",EDGE,"E116"),sQuery(id+"F0.wireOp",EDGE,"E117"),sQuery(id+"F0.wireOp",EDGE,"E118"),sQuery(id+"F0.wireOp",EDGE,"E119"),sQuery(id+"F0.wireOp",EDGE,"E120"),sQuery(id+"F0.wireOp",EDGE,"E121"),sQuery(id+"F0.wireOp",EDGE,"E122"),sQuery(id+"F0.wireOp",EDGE,"E123"),sQuery(id+"F0.wireOp",EDGE,"E124"),sQuery(id+"F0.wireOp",EDGE,"E125"),sQuery(id+"F0.wireOp",EDGE,"E126"),sQuery(id+"F0.wireOp",EDGE,"E127"),sQuery(id+"F0.wireOp",EDGE,"E128"),sQuery(id+"F0.wireOp",EDGE,"E129"),sQuery(id+"F0.wireOp",EDGE,"E130")])]});
            var Q6;
            Q6=makeQuery(id+"F2.opExtrude","SWEPT_BODY",BODY,{"disambiguationData":[OSD([sQuery(id+"F0.wireOp",EDGE,"E131"),sQuery(id+"F0.wireOp",EDGE,"E132"),sQuery(id+"F0.wireOp",EDGE,"E133"),sQuery(id+"F0.wireOp",EDGE,"E134"),sQuery(id+"F0.wireOp",EDGE,"E135"),sQuery(id+"F0.wireOp",EDGE,"E136"),sQuery(id+"F0.wireOp",EDGE,"E137"),sQuery(id+"F0.wireOp",EDGE,"E138"),sQuery(id+"F0.wireOp",EDGE,"E139"),sQuery(id+"F0.wireOp",EDGE,"E140"),sQuery(id+"F0.wireOp",EDGE,"E141"),sQuery(id+"F0.wireOp",EDGE,"E142"),sQuery(id+"F0.wireOp",EDGE,"E143"),sQuery(id+"F0.wireOp",EDGE,"E144"),sQuery(id+"F0.wireOp",EDGE,"E145"),sQuery(id+"F0.wireOp",EDGE,"E146"),sQuery(id+"F0.wireOp",EDGE,"E147"),sQuery(id+"F0.wireOp",EDGE,"E148"),sQuery(id+"F0.wireOp",EDGE,"E149"),sQuery(id+"F0.wireOp",EDGE,"E150"),sQuery(id+"F0.wireOp",EDGE,"E151"),sQuery(id+"F0.wireOp",EDGE,"E152")])]});
            var Q7;
            Q7=makeQuery(id+"F2.opExtrude","SWEPT_BODY",BODY,{"disambiguationData":[OSD([sQuery(id+"F0.wireOp",EDGE,"E157"),sQuery(id+"F0.wireOp",EDGE,"E158"),sQuery(id+"F0.wireOp",EDGE,"E159"),sQuery(id+"F0.wireOp",EDGE,"E160"),sQuery(id+"F0.wireOp",EDGE,"E161"),sQuery(id+"F0.wireOp",EDGE,"E162"),sQuery(id+"F0.wireOp",EDGE,"E163"),sQuery(id+"F0.wireOp",EDGE,"E164"),sQuery(id+"F0.wireOp",EDGE,"E165"),sQuery(id+"F0.wireOp",EDGE,"E166"),sQuery(id+"F0.wireOp",EDGE,"E167"),sQuery(id+"F0.wireOp",EDGE,"E168"),sQuery(id+"F0.wireOp",EDGE,"E169"),sQuery(id+"F0.wireOp",EDGE,"E170"),sQuery(id+"F0.wireOp",EDGE,"E171"),sQuery(id+"F0.wireOp",EDGE,"E172"),sQuery(id+"F0.wireOp",EDGE,"E173"),sQuery(id+"F0.wireOp",EDGE,"E174"),sQuery(id+"F0.wireOp",EDGE,"E175"),sQuery(id+"F0.wireOp",EDGE,"E176"),sQuery(id+"F0.wireOp",EDGE,"E177"),sQuery(id+"F0.wireOp",EDGE,"E178"),sQuery(id+"F0.wireOp",EDGE,"E179"),sQuery(id+"F0.wireOp",EDGE,"E180"),sQuery(id+"F0.wireOp",EDGE,"E181"),sQuery(id+"F0.wireOp",EDGE,"E182"),sQuery(id+"F0.wireOp",EDGE,"E183"),sQuery(id+"F0.wireOp",EDGE,"E184"),sQuery(id+"F0.wireOp",EDGE,"E185"),sQuery(id+"F0.wireOp",EDGE,"E186"),sQuery(id+"F0.wireOp",EDGE,"E187")])]});
            var Q8;
            Q8=makeQuery(id+"F2.opExtrude","SWEPT_BODY",BODY,{"disambiguationData":[OSD([sQuery(id+"F0.wireOp",EDGE,"E188"),sQuery(id+"F0.wireOp",EDGE,"E189"),sQuery(id+"F0.wireOp",EDGE,"E190"),sQuery(id+"F0.wireOp",EDGE,"E191"),sQuery(id+"F0.wireOp",EDGE,"E192"),sQuery(id+"F0.wireOp",EDGE,"E193"),sQuery(id+"F0.wireOp",EDGE,"E194"),sQuery(id+"F0.wireOp",EDGE,"E195"),sQuery(id+"F0.wireOp",EDGE,"E196"),sQuery(id+"F0.wireOp",EDGE,"E197"),sQuery(id+"F0.wireOp",EDGE,"E198"),sQuery(id+"F0.wireOp",EDGE,"E199"),sQuery(id+"F0.wireOp",EDGE,"E200"),sQuery(id+"F0.wireOp",EDGE,"E201"),sQuery(id+"F0.wireOp",EDGE,"E202"),sQuery(id+"F0.wireOp",EDGE,"E203"),sQuery(id+"F0.wireOp",EDGE,"E204"),sQuery(id+"F0.wireOp",EDGE,"E205"),sQuery(id+"F0.wireOp",EDGE,"E206"),sQuery(id+"F0.wireOp",EDGE,"E207"),sQuery(id+"F0.wireOp",EDGE,"E208"),sQuery(id+"F0.wireOp",EDGE,"E209")])]});
            var Q9;
            Q9=makeQuery(id+"F1.opExtrude","SWEPT_BODY",BODY,{"disambiguationData":[OSD([sQuery(id+"F0.wireOp",EDGE,"E217"),sQuery(id+"F0.wireOp",EDGE,"E218"),sQuery(id+"F0.wireOp",EDGE,"E219"),sQuery(id+"F0.wireOp",EDGE,"E220"),sQuery(id+"F0.wireOp",EDGE,"E221"),sQuery(id+"F0.wireOp",EDGE,"E222"),sQuery(id+"F0.wireOp",EDGE,"E223"),sQuery(id+"F0.wireOp",EDGE,"E224")])]});
            var Q10;
            Q10=makeQuery(id+"F1.opExtrude","SWEPT_BODY",BODY,{"disambiguationData":[OSD([sQuery(id+"F0.wireOp",EDGE,"E225"),sQuery(id+"F0.wireOp",EDGE,"E226"),sQuery(id+"F0.wireOp",EDGE,"E227"),sQuery(id+"F0.wireOp",EDGE,"E228"),sQuery(id+"F0.wireOp",EDGE,"E229"),sQuery(id+"F0.wireOp",EDGE,"E230"),sQuery(id+"F0.wireOp",EDGE,"E231"),sQuery(id+"F0.wireOp",EDGE,"E232"),sQuery(id+"F0.wireOp",EDGE,"E233"),sQuery(id+"F0.wireOp",EDGE,"E234"),sQuery(id+"F0.wireOp",EDGE,"E235"),sQuery(id+"F0.wireOp",EDGE,"E236"),sQuery(id+"F0.wireOp",EDGE,"E237"),sQuery(id+"F0.wireOp",EDGE,"E238")])]});
            var Q11;
            Q11=makeQuery(id+"F1.opExtrude","SWEPT_BODY",BODY,{"disambiguationData":[OSD([sQuery(id+"F0.wireOp",EDGE,"E239"),sQuery(id+"F0.wireOp",EDGE,"E240"),sQuery(id+"F0.wireOp",EDGE,"E241"),sQuery(id+"F0.wireOp",EDGE,"E242")])]});
            var Q12;
            Q12=makeQuery(id+"F1.opExtrude","SWEPT_BODY",BODY,{"disambiguationData":[OSD([sQuery(id+"F0.wireOp",EDGE,"E243"),sQuery(id+"F0.wireOp",EDGE,"E244"),sQuery(id+"F0.wireOp",EDGE,"E245"),sQuery(id+"F0.wireOp",EDGE,"E246"),sQuery(id+"F0.wireOp",EDGE,"E247"),sQuery(id+"F0.wireOp",EDGE,"E248"),sQuery(id+"F0.wireOp",EDGE,"E249"),sQuery(id+"F0.wireOp",EDGE,"E250"),sQuery(id+"F0.wireOp",EDGE,"E251"),sQuery(id+"F0.wireOp",EDGE,"E252"),sQuery(id+"F0.wireOp",EDGE,"E253"),sQuery(id+"F0.wireOp",EDGE,"E254"),sQuery(id+"F0.wireOp",EDGE,"E255"),sQuery(id+"F0.wireOp",EDGE,"E256"),sQuery(id+"F0.wireOp",EDGE,"E257"),sQuery(id+"F0.wireOp",EDGE,"E258"),sQuery(id+"F0.wireOp",EDGE,"E259"),sQuery(id+"F0.wireOp",EDGE,"E260"),sQuery(id+"F0.wireOp",EDGE,"E261")])]});
            var Q13;
            Q13=makeQuery(id+"F1.opExtrude","SWEPT_BODY",BODY,{"disambiguationData":[OSD([sQuery(id+"F0.wireOp",EDGE,"E262"),sQuery(id+"F0.wireOp",EDGE,"E263"),sQuery(id+"F0.wireOp",EDGE,"E264"),sQuery(id+"F0.wireOp",EDGE,"E265"),sQuery(id+"F0.wireOp",EDGE,"E266"),sQuery(id+"F0.wireOp",EDGE,"E267"),sQuery(id+"F0.wireOp",EDGE,"E268"),sQuery(id+"F0.wireOp",EDGE,"E269"),sQuery(id+"F0.wireOp",EDGE,"E270"),sQuery(id+"F0.wireOp",EDGE,"E271"),sQuery(id+"F0.wireOp",EDGE,"E272"),sQuery(id+"F0.wireOp",EDGE,"E291"),sQuery(id+"F0.wireOp",EDGE,"E292"),sQuery(id+"F0.wireOp",EDGE,"E293"),sQuery(id+"F0.wireOp",EDGE,"E294"),sQuery(id+"F0.wireOp",EDGE,"E295"),sQuery(id+"F0.wireOp",EDGE,"E296"),sQuery(id+"F0.wireOp",EDGE,"E297"),sQuery(id+"F0.wireOp",EDGE,"E298")])]});
            var Q14;
            Q14=makeQuery(id+"F1.opExtrude","SWEPT_BODY",BODY,{"disambiguationData":[OSD([sQuery(id+"F0.wireOp",EDGE,"E273"),sQuery(id+"F0.wireOp",EDGE,"E274"),sQuery(id+"F0.wireOp",EDGE,"E275"),sQuery(id+"F0.wireOp",EDGE,"E276"),sQuery(id+"F0.wireOp",EDGE,"E277"),sQuery(id+"F0.wireOp",EDGE,"E278"),sQuery(id+"F0.wireOp",EDGE,"E279"),sQuery(id+"F0.wireOp",EDGE,"E280"),sQuery(id+"F0.wireOp",EDGE,"E281"),sQuery(id+"F0.wireOp",EDGE,"E282"),sQuery(id+"F0.wireOp",EDGE,"E283"),sQuery(id+"F0.wireOp",EDGE,"E284"),sQuery(id+"F0.wireOp",EDGE,"E285"),sQuery(id+"F0.wireOp",EDGE,"E286"),sQuery(id+"F0.wireOp",EDGE,"E287"),sQuery(id+"F0.wireOp",EDGE,"E288"),sQuery(id+"F0.wireOp",EDGE,"E289"),sQuery(id+"F0.wireOp",EDGE,"E290")])]});
            var Q15;
            Q15=makeQuery(id+"F5.opExtrude","SWEPT_BODY",BODY,{"disambiguationData":[OSD([sQuery(id+"F4.wireOp",EDGE,"E299.rect.top"),sQuery(id+"F4.wireOp",EDGE,"E299.rect.left"),sQuery(id+"F4.wireOp",EDGE,"E299.rect.right"),sQuery(id+"F4.wireOp",EDGE,"E300"),sQuery(id+"F4.wireOp",EDGE,"E303.filletArc"),sQuery(id+"F4.wireOp",EDGE,"E304.filletArc"),sQuery(id+"F4.wireOp",EDGE,"E305.filletArc"),sQuery(id+"F4.wireOp",EDGE,"E306.filletArc")])]});
            booleanBodies(context, id + "F7", {"operationType" : BooleanOperationType.SUBTRACTION, "tools" : qUnion([Q0, Q1, Q2, Q3, Q4, Q5, Q6, Q7, Q8, Q9, Q10, Q11, Q12, Q13, Q14]), "targets" : qUnion([Q15]), "offset" : true, "offsetAll" : true, "offsetDistance" : .3 * mm, "keepTools" : true});
        }
        {
            var Q0;
            Q0=makeQuery(id+"F5.opExtrude","CAP_EDGE",EDGE,{"disambiguationData":[OSD([sQuery(id+"F4.wireOp",EDGE,"E300")])],"isStart":true});
            fillet(context, id + "F8", {"entities" : qUnion([Q0]), "radius" : 5 * mm, "tangentPropagation" : true, "allowEdgeOverflow" : false});
        }
    });
